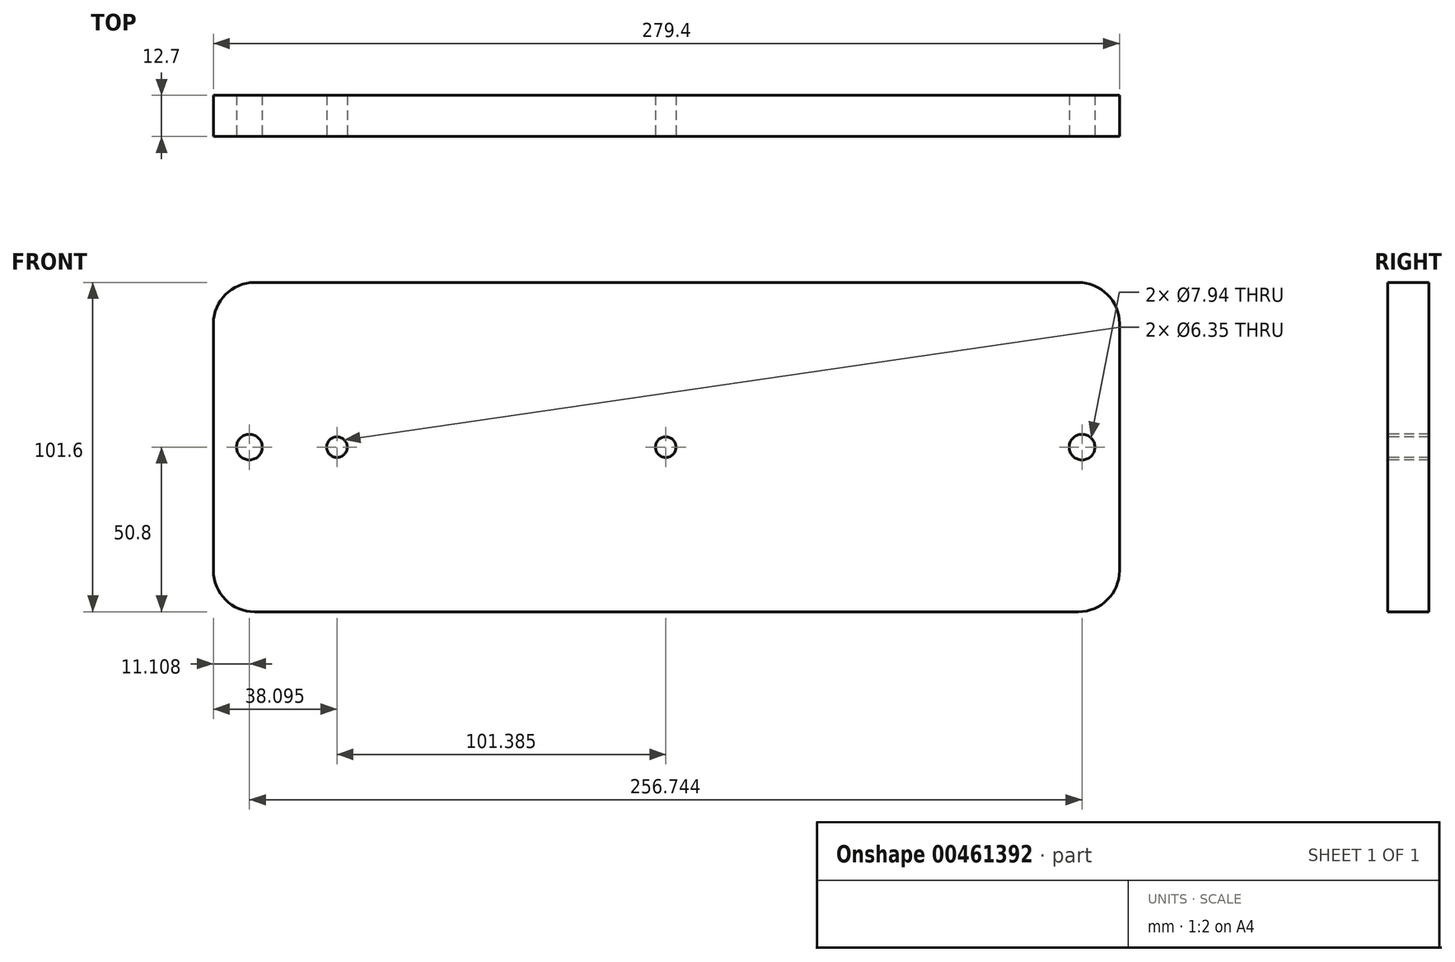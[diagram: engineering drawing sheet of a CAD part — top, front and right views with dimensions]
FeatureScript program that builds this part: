
annotation { "Feature Type Name" : "Feature", "Feature Type Description" : "" }
export const myFeature = defineFeature(function(context is Context, id is Id, definition is map)
    precondition{}
    {
        {
            var Q0;
            Q0=qCreatedBy(makeId("Front.planeOp"),FACE);
            var sketch = newSketch(context, id + "F0", { "sketchPlane" : qUnion([Q0])});
            skLineSegment(sketch, "E0", {"start": v(-126.78, 50.8) * mm, "end": v(127.22, 50.8) * mm});
            skLineSegment(sketch, "E1", {"start": v(-139.48, 38.1) * mm, "end": v(-139.48, -38.1) * mm});
            skLineSegment(sketch, "E2", {"start": v(-126.78, -50.8) * mm, "end": v(127.22, -50.8) * mm});
            skLineSegment(sketch, "E3", {"start": v(139.92, 38.1) * mm, "end": v(139.92, -38.1) * mm});
            skPoint(sketch, "E4.visualSharp", {"position": v(-139.48, 50.8) * mm});
            skArc(sketch, "E4.filletArc", {"start": v(-126.78, 50.8) * mm, "mid": v(-135.76, 47.08) * mm, "end": v(-139.48, 38.1) * mm});
            skPoint(sketch, "E5.visualSharp", {"position": v(-139.48, -50.8) * mm});
            skArc(sketch, "E5.filletArc", {"start": v(-139.48, -38.1) * mm, "mid": v(-135.76, -47.08) * mm, "end": v(-126.78, -50.8) * mm});
            skPoint(sketch, "E6.visualSharp", {"position": v(139.92, 50.8) * mm});
            skArc(sketch, "E6.filletArc", {"start": v(139.92, 38.1) * mm, "mid": v(136.2, 47.08) * mm, "end": v(127.22, 50.8) * mm});
            skPoint(sketch, "E7.visualSharp", {"position": v(139.92, -50.8) * mm});
            skArc(sketch, "E7.filletArc", {"start": v(127.22, -50.8) * mm, "mid": v(136.2, -47.08) * mm, "end": v(139.92, -38.1) * mm});
            skLineSegment(sketch, "E8", {"start": v(219.64, 0) * mm, "end": v(-135.76, 0) * mm, "construction": true});
            skPoint(sketch, "E8.startSnap0", {"position": v(-139.48, 0) * mm});
            skPoint(sketch, "E8.endSnap0", {"position": v(-135.76, -47.08) * mm});
            skPoint(sketch, "E9", {"position": v(-128.37, 0) * mm});
            skPoint(sketch, "E10", {"position": v(-101.38, 0) * mm});
            skLineSegment(sketch, "E11", {"start": v(-139.48, 0) * mm, "end": v(0.22, 0) * mm, "construction": true});
            skLineSegment(sketch, "E12", {"start": v(0.22, 44.37) * mm, "end": v(0.22, -120.5) * mm, "construction": true});
            skPoint(sketch, "E12.startSnap0", {"position": v(0.22, 50.8) * mm});
            skPoint(sketch, "E12.endSnap0", {"position": v(0.22, -50.8) * mm});
            skPoint(sketch, "E13.MirrorP", {"position": v(128.8, 0) * mm});
            skPoint(sketch, "E14", {"position": v(0.22, 0) * mm});
            skSolve(sketch);
        }
        {
            var Q0;
            Q0=makeQuery(id+"F0.imprint","IMPRINT",FACE,{"disambiguationData":[TD([[makeQuery(id+"F0.imprint","IMPRINT",EDGE,{"derivedFrom":sQuery(id+"F0.wireOp",EDGE,"E0")}),-1.0]])]});
            extrude(context, id + "F1", {"entities" : qUnion([Q0]), "depth" : 12.7 * mm});
        }
        {
            var Q0;
            Q0=makeQuery(id+"F1.opExtrude","CAP_FACE",FACE,{"disambiguationData":[OSD([sQuery(id+"F0.wireOp",EDGE,"E0"),sQuery(id+"F0.wireOp",EDGE,"E1"),sQuery(id+"F0.wireOp",EDGE,"E2"),sQuery(id+"F0.wireOp",EDGE,"E3"),sQuery(id+"F0.wireOp",EDGE,"E4.filletArc"),sQuery(id+"F0.wireOp",EDGE,"E5.filletArc"),sQuery(id+"F0.wireOp",EDGE,"E6.filletArc"),sQuery(id+"F0.wireOp",EDGE,"E7.filletArc")])],"isStart":false});
            var sketch = newSketch(context, id + "F2", { "sketchPlane" : qUnion([Q0])});
            skLineSegment(sketch, "E15", {"start": v(-139.48, 0) * mm, "end": v(-139.48, 50.8) * mm, "construction": true});
            skLineSegment(sketch, "E16", {"start": v(-139.48, 0) * mm, "end": v(-128.37, 0) * mm, "construction": true});
            skPoint(sketch, "E17", {"position": v(-128.37, 0) * mm});
            skLineSegment(sketch, "E18", {"start": v(-139.48, 0) * mm, "end": v(-101.38, 0) * mm, "construction": true});
            skPoint(sketch, "E19", {"position": v(-101.38, 0) * mm});
            skPoint(sketch, "E20", {"position": v(0, 0) * mm});
            skLineSegment(sketch, "E21", {"start": v(0, 90.9) * mm, "end": v(0, -132.9) * mm, "construction": true});
            skPoint(sketch, "E22.MirrorP", {"position": v(128.37, 0) * mm});
            skSolve(sketch);
        }
        {
            var Q0;
            Q0=sQuery(id+"F2.wireOp",VERTEX,"E16.end");
            var Q1;
            Q1=sQuery(id+"F2.wireOp",VERTEX,"E22.MirrorP");
            var Q2;
            Q2=makeQuery(id+"F1.opExtrude","SWEPT_BODY",BODY,{"disambiguationData":[OSD([sQuery(id+"F0.wireOp",EDGE,"E0"),sQuery(id+"F0.wireOp",EDGE,"E1"),sQuery(id+"F0.wireOp",EDGE,"E2"),sQuery(id+"F0.wireOp",EDGE,"E3"),sQuery(id+"F0.wireOp",EDGE,"E4.filletArc"),sQuery(id+"F0.wireOp",EDGE,"E5.filletArc"),sQuery(id+"F0.wireOp",EDGE,"E6.filletArc"),sQuery(id+"F0.wireOp",EDGE,"E7.filletArc")])]});
            hole(context, id + "F3", {"style" : HoleStyle.SIMPLE, "endStyle" : HoleEndStyle.THROUGH, "holeDiameter" : 7.94 * mm, "isTappedThrough" : true, "tappedDepth" : 12.7 * mm, "tapClearance" : 3, "locations" : qUnion([Q0, Q1]), "scope" : qUnion([Q2])});
        }
        {
            var Q0;
            Q0=makeQuery(id+"F1.opExtrude","CAP_FACE",FACE,{"disambiguationData":[OSD([sQuery(id+"F0.wireOp",EDGE,"E0"),sQuery(id+"F0.wireOp",EDGE,"E1"),sQuery(id+"F0.wireOp",EDGE,"E2"),sQuery(id+"F0.wireOp",EDGE,"E3"),sQuery(id+"F0.wireOp",EDGE,"E4.filletArc"),sQuery(id+"F0.wireOp",EDGE,"E5.filletArc"),sQuery(id+"F0.wireOp",EDGE,"E6.filletArc"),sQuery(id+"F0.wireOp",EDGE,"E7.filletArc")])],"isStart":false});
            var sketch = newSketch(context, id + "F4", { "sketchPlane" : qUnion([Q0])});
            skLineSegment(sketch, "E23", {"start": v(-139.48, 0) * mm, "end": v(-101.38, 0) * mm, "construction": true});
            skPoint(sketch, "E23.endSnap0", {"position": v(-139.48, 0) * mm});
            skLineSegment(sketch, "E24", {"start": v(139.92, 0) * mm, "end": v(101.82, 0) * mm, "construction": true});
            skSolve(sketch);
        }
        {
            var Q0;
            Q0=sQuery(id+"F4.wireOp",VERTEX,"E23.end");
            var Q1;
            Q1=makeQuery(id+"F1.opExtrude","SWEPT_BODY",BODY,{"disambiguationData":[OSD([sQuery(id+"F0.wireOp",EDGE,"E0"),sQuery(id+"F0.wireOp",EDGE,"E1"),sQuery(id+"F0.wireOp",EDGE,"E2"),sQuery(id+"F0.wireOp",EDGE,"E3"),sQuery(id+"F0.wireOp",EDGE,"E4.filletArc"),sQuery(id+"F0.wireOp",EDGE,"E5.filletArc"),sQuery(id+"F0.wireOp",EDGE,"E6.filletArc"),sQuery(id+"F0.wireOp",EDGE,"E7.filletArc")])]});
            hole(context, id + "F5", {"style" : HoleStyle.SIMPLE, "endStyle" : HoleEndStyle.THROUGH, "holeDiameter" : 6.35 * mm, "isTappedThrough" : true, "tappedDepth" : 12.7 * mm, "tapClearance" : 3, "locations" : qUnion([Q0]), "scope" : qUnion([Q1])});
        }
        {
            var Q0;
            Q0=makeQuery(id+"F1.opExtrude","CAP_FACE",FACE,{"disambiguationData":[OSD([sQuery(id+"F0.wireOp",EDGE,"E0"),sQuery(id+"F0.wireOp",EDGE,"E1"),sQuery(id+"F0.wireOp",EDGE,"E2"),sQuery(id+"F0.wireOp",EDGE,"E3"),sQuery(id+"F0.wireOp",EDGE,"E4.filletArc"),sQuery(id+"F0.wireOp",EDGE,"E5.filletArc"),sQuery(id+"F0.wireOp",EDGE,"E6.filletArc"),sQuery(id+"F0.wireOp",EDGE,"E7.filletArc")])],"isStart":false});
            var sketch = newSketch(context, id + "F6", { "sketchPlane" : qUnion([Q0])});
            skPoint(sketch, "E25", {"position": v(0, 0) * mm});
            skSolve(sketch);
        }
        {
            var Q0;
            Q0=sQuery(id+"F6.wireOp",VERTEX,"E25");
            var Q1;
            Q1=makeQuery(id+"F1.opExtrude","SWEPT_BODY",BODY,{"disambiguationData":[OSD([sQuery(id+"F0.wireOp",EDGE,"E0"),sQuery(id+"F0.wireOp",EDGE,"E1"),sQuery(id+"F0.wireOp",EDGE,"E2"),sQuery(id+"F0.wireOp",EDGE,"E3"),sQuery(id+"F0.wireOp",EDGE,"E4.filletArc"),sQuery(id+"F0.wireOp",EDGE,"E5.filletArc"),sQuery(id+"F0.wireOp",EDGE,"E6.filletArc"),sQuery(id+"F0.wireOp",EDGE,"E7.filletArc")])]});
            hole(context, id + "F7", {"style" : HoleStyle.SIMPLE, "endStyle" : HoleEndStyle.THROUGH, "holeDiameter" : 6.35 * mm, "isTappedThrough" : true, "tappedDepth" : 12.7 * mm, "tapClearance" : 3, "locations" : qUnion([Q0]), "scope" : qUnion([Q1])});
        }
    });
